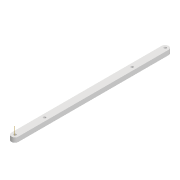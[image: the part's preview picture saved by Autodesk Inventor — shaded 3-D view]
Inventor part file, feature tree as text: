
AUTODESK INVENTOR PART (.ipt)
format: ipt  version: 2022 (Build 260153000, 153)  size: 93,696 bytes
history: native  units: mm
features: extrude x1, other x1, sketch x1
ambient origin geometry x8: Origin, YZ Plane, XZ Plane, XY Plane, X Axis, Y Axis, Z Axis, Center Point
bodies: Solid1 (feature_tree)
feature tree (3):
  extrude  "Extrusion1"  Depth=101.165mm
  other  "Work Axis2"
  sketch  "Sketch1"  dims[d0=2.2mm d1=2.2mm d2=6.0mm d3=129.784mm d4=2.2mm d5=25.613mm d6=4.0mm d7=0.0mm d8=2.2mm d9=101.165mm]
